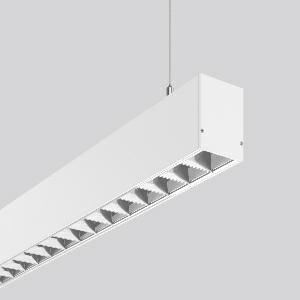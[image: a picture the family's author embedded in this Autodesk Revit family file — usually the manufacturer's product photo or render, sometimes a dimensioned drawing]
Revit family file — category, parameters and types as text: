
# Revit family: less_is_more_50_312339_002_1_c40b
name_source: partatom
category: Lighting Fixtures
units: mm (PartAtom-declared; Revit-internal decimal feet)

## family parameters
Cut with Voids When Loaded = No
Host = Face
Light Source = No
Part Type = Normal
Room Calculation Point = No
Round Connector Dimension = Use Diameter
Shared = No

## types (1)
- LESS IS MORE 50 (1 x LED Modul 840, 6200 lm, 4000)
    Apparent Load = 48 VA
    CIE Flux Codes = 95 100 100 100 100
    Color Rendering = 80
    Color Temperature = 4000
    Default Elevation = 1800 mm
    Description = Series: LESS IS MORE 50
Linear pendant luminaire for aesthetically sophisticated lighting. Housing: extruded aluminium profile, powder-coated. End cap aluminium powder-coated. Canopy made of aluminium, powder-coated. Alea optical system: Reflector structure (ABS, Aluminium-coated, highly polished) with integrated diffuser made of non-yellowing plastic (PMMA) opal for glare-free light at the workstation (screen-compliant according to EN 12464-1). Direct light emission. Suitable for pendant. 2-point steel cable suspension freely positionable and infinitely height-adjustable. Special lengths available on request. LED unit with integrated converter interchangeable and removable. Suitable for through-wiring. With sensors or as a safety luminaire on request. 
Colour: traffic white, matt (RAL 9016)
Length: 1967 mm
Width: 57 mm
Height: 75 mm
Suspension length: 2000 mm
Lamp: LED
Socket: without socket
Colour temperature: 4000K
Colour rendering index (CRI): 80
System power: 48 W
Rated luminous flux: 6200 lm
Luminous efficiency: 129 lm/W
Control gear: Regulated power supply
Protection class: I
Type of protection: IP 20
    Height = 75 mm
    Lamp = 1 x LED Modul 840
    Lamp Light Flux = 6200 lm
    Lamp count = 1
    Length = 1967 mm
    Lifetime = 50000 h
    Luminous efficacy = 129 lm/W
    Manufacturer = RZB
    ModVariant = No
    Model = 312339.002.1
    Mounting Place = Ceiling
    Mounting Type = Pendant
    Number of Poles = 1
    OnlyDefault = Yes
    Power Factor = 1
    Product Name = LESS IS MORE 50
    Product group = Pendant LED linear luminaires
    ProductGroupID = 907
    Protection Class = Protection class I
    Protection Degree = IP 20
    RLX_Detail_Level = 1
    RLX_Emergency_Light_Flux = 0 lm
    RLX_Emergency_Type = 0
    RLX_Emergency_Type_DB = No
    RlxData = <blob elided: 33117 chars, md5=d575a2f9>
    Socket = socket
    Standby Power = 0 W
    System Light Flux = 6200 lm
    System Power = 48 W
    Type Comments = Product without accessories
    Type Image = 312342.002.jpg
    URL = http://relux.com
    VarID = ---
    Voltage = 230 V
    Voltage Range = 220-240 V
    Weight = 0.00 kg
    Width = 57 mm

## geometry (parser evidence)
native form markers: Blend x4, Sweep x9
no freeform markers — native parametric forms only
